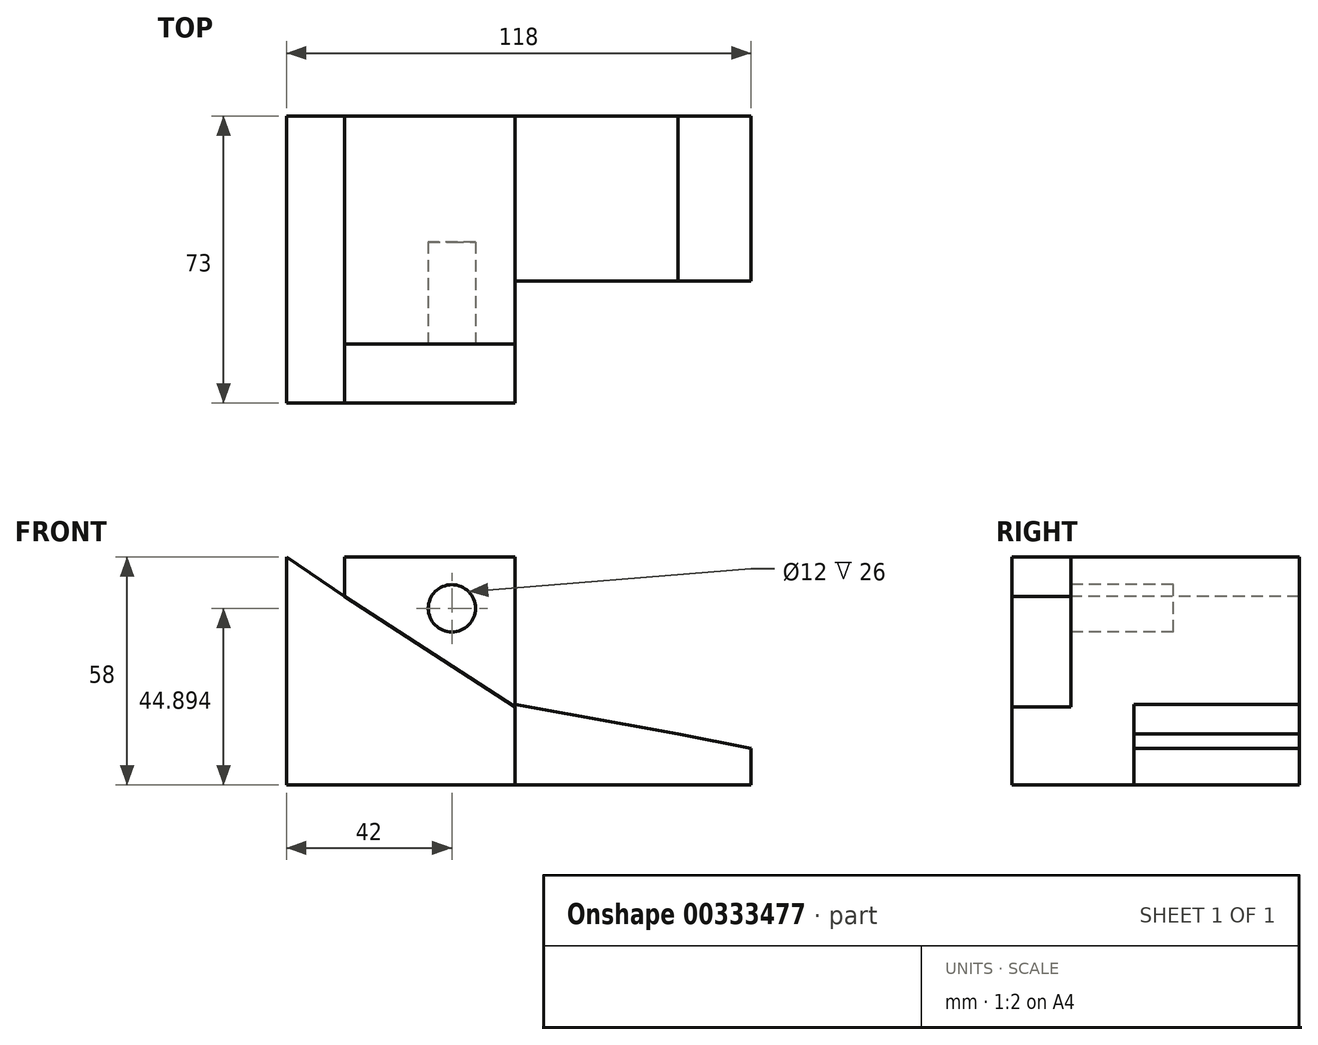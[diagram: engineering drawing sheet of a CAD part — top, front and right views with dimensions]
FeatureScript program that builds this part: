
annotation { "Feature Type Name" : "Feature", "Feature Type Description" : "" }
export const myFeature = defineFeature(function(context is Context, id is Id, definition is map)
    precondition{}
    {
        {
            var Q0;
            Q0=qCreatedBy(makeId("Top.planeOp"),FACE);
            var sketch = newSketch(context, id + "F0", { "sketchPlane" : qUnion([Q0])});
            skLineSegment(sketch, "E0", {"start": v(0, 0) * mm, "end": v(0, 58) * mm});
            skLineSegment(sketch, "E1", {"start": v(0, 58) * mm, "end": v(118, 58) * mm});
            skLineSegment(sketch, "E2", {"start": v(118, 58) * mm, "end": v(118, 16) * mm});
            skLineSegment(sketch, "E3", {"start": v(118, 16) * mm, "end": v(88, 16) * mm});
            skLineSegment(sketch, "E4", {"start": v(88, 16) * mm, "end": v(88, 42) * mm});
            skLineSegment(sketch, "E5", {"start": v(88, 42) * mm, "end": v(16, 42) * mm});
            skLineSegment(sketch, "E6", {"start": v(16, 42) * mm, "end": v(16, 16) * mm});
            skLineSegment(sketch, "E7", {"start": v(16, 16) * mm, "end": v(88, 16) * mm});
            skLineSegment(sketch, "E8", {"start": v(58, 16) * mm, "end": v(58, 0) * mm});
            skLineSegment(sketch, "E9", {"start": v(58, 0) * mm, "end": v(0, 0) * mm});
            skSolve(sketch);
        }
        {
            var Q0;
            Q0 = qSketchRegion(id + "F0", true);
            extrude(context, id + "F1", {"entities" : qUnion([Q0]), "depth" : 58 * mm});
        }
        {
            var Q0;
            Q0=makeQuery(id+"F1.opExtrude","SWEPT_FACE",FACE,{"disambiguationData":[OSD([sQuery(id+"F0.wireOp",EDGE,"E9")])]});
            var sketch = newSketch(context, id + "F2", { "sketchPlane" : qUnion([Q0])});
            skLineSegment(sketch, "E10", {"start": v(0, 58) * mm, "end": v(14.69, 58) * mm});
            skLineSegment(sketch, "E11", {"start": v(14.69, 58) * mm, "end": v(14.69, 47.95) * mm});
            skLineSegment(sketch, "E12", {"start": v(14.69, 47.95) * mm, "end": v(0, 58) * mm});
            skSolve(sketch);
        }
        {
            var Q0;
            Q0 = qSketchRegion(id + "F2", true);
            extrude(context, id + "F3", {"entities" : qUnion([Q0]), "operationType" : NewBodyOperationType.REMOVE, "endBound" : BoundingType.THROUGH_ALL, "oppositeDirection" : true, "depth" : 0.5 * mm});
        }
        {
            var Q0;
            Q0=makeQuery(id+"F1.opExtrude","SWEPT_FACE",FACE,{"disambiguationData":[OSD([sQuery(id+"F0.wireOp",EDGE,"E9")])]});
            var sketch = newSketch(context, id + "F4", { "sketchPlane" : qUnion([Q0])});
            skLineSegment(sketch, "E13", {"start": v(14.69, 47.95) * mm, "end": v(58, 19.88) * mm});
            skLineSegment(sketch, "E14", {"start": v(58, 19.88) * mm, "end": v(58, 0) * mm});
            skLineSegment(sketch, "E15", {"start": v(58, 0) * mm, "end": v(0, 0) * mm});
            skLineSegment(sketch, "E16", {"start": v(0, 0) * mm, "end": v(0, 58) * mm});
            skLineSegment(sketch, "E17", {"start": v(0, 58) * mm, "end": v(14.69, 47.95) * mm});
            skLineSegment(sketch, "E18", {"start": v(58, 19.88) * mm, "end": v(117.83, 10.04) * mm});
            skLineSegment(sketch, "E19", {"start": v(117.83, 10.04) * mm, "end": v(117.83, 0) * mm});
            skLineSegment(sketch, "E20", {"start": v(117.83, 0) * mm, "end": v(58, 0) * mm});
            skSolve(sketch);
        }
        {
            var Q0;
            Q0=makeQuery(id+"F1.opExtrude","SWEPT_FACE",FACE,{"disambiguationData":[OSD([sQuery(id+"F0.wireOp",EDGE,"E3"),sQuery(id+"F0.wireOp",EDGE,"E7")])]});
            var sketch = newSketch(context, id + "F5", { "sketchPlane" : qUnion([Q0])});
            skLineSegment(sketch, "E21", {"start": v(97.53, 58) * mm, "end": v(99.47, 12.93) * mm});
            skLineSegment(sketch, "E22", {"start": v(99.47, 12.93) * mm, "end": v(118, 9.31) * mm});
            skLineSegment(sketch, "E23", {"start": v(118, 9.31) * mm, "end": v(118, 58) * mm});
            skLineSegment(sketch, "E24", {"start": v(118, 58) * mm, "end": v(97.53, 58) * mm});
            skSolve(sketch);
        }
        {
            var Q0;
            Q0=makeQuery(id+"F5.imprint","IMPRINT",FACE,{"disambiguationData":[TD([[makeQuery(id+"F5.imprint","IMPRINT",EDGE,{"derivedFrom":sQuery(id+"F5.wireOp",EDGE,"E21")}),1.0]])]});
            extrude(context, id + "F6", {"entities" : qUnion([Q0]), "operationType" : NewBodyOperationType.REMOVE, "endBound" : BoundingType.THROUGH_ALL, "oppositeDirection" : true, "depth" : 25 * mm});
        }
        {
            var Q0;
            Q0=makeQuery(id+"F4.imprint","IMPRINT",FACE,{"disambiguationData":[TD([[makeQuery(id+"F4.imprint","IMPRINT",EDGE,{"derivedFrom":sQuery(id+"F4.wireOp",EDGE,"E13")}),-1.0]])]});
            extrude(context, id + "F7", {"entities" : qUnion([Q0]), "operationType" : NewBodyOperationType.ADD, "endBound" : BoundingType.SYMMETRIC, "depth" : 30 * mm});
        }
        {
            var Q0;
            Q0=makeQuery(id+"F1.opExtrude","SWEPT_FACE",FACE,{"disambiguationData":[OSD([sQuery(id+"F0.wireOp",EDGE,"E3"),sQuery(id+"F0.wireOp",EDGE,"E7")])]});
            var sketch = newSketch(context, id + "F8", { "sketchPlane" : qUnion([Q0])});
            skLineSegment(sketch, "E25", {"start": v(58, 58) * mm, "end": v(58, 20.43) * mm});
            skLineSegment(sketch, "E26", {"start": v(58, 20.43) * mm, "end": v(99.47, 12.93) * mm});
            skLineSegment(sketch, "E27", {"start": v(99.47, 12.93) * mm, "end": v(97.53, 58) * mm});
            skLineSegment(sketch, "E28", {"start": v(97.53, 58) * mm, "end": v(58, 58) * mm});
            skSolve(sketch);
        }
        {
            var Q0;
            Q0 = qSketchRegion(id + "F8", true);
            extrude(context, id + "F9", {"entities" : qUnion([Q0]), "operationType" : NewBodyOperationType.REMOVE, "endBound" : BoundingType.THROUGH_ALL, "oppositeDirection" : true, "depth" : 25 * mm});
        }
        {
            var Q0;
            Q0=makeQuery(id+"F1.opExtrude","SWEPT_FACE",FACE,{"disambiguationData":[OSD([sQuery(id+"F0.wireOp",EDGE,"E9")])]});
            var sketch = newSketch(context, id + "F10", { "sketchPlane" : qUnion([Q0])});
            skCircle(sketch, "E29", {"center": v(42, 44.9) * mm, "radius": 6 * mm});
            skSolve(sketch);
        }
        {
            var Q0;
            Q0=makeQuery(id+"F10.imprint","IMPRINT",FACE,{"disambiguationData":[TD([[makeQuery(id+"F10.imprint","IMPRINT",EDGE,{"derivedFrom":sQuery(id+"F10.wireOp",EDGE,"E29")}),1.0]])]});
            var Q1;
            Q1=sQuery(id+"F10.wireOp",EDGE,"E29");
            extrude(context, id + "F11", {"entities" : qUnion([Q0]), "operationType" : NewBodyOperationType.REMOVE, "surfaceEntities" : qUnion([Q1]), "oppositeDirection" : true, "depth" : 26 * mm});
        }
    });
